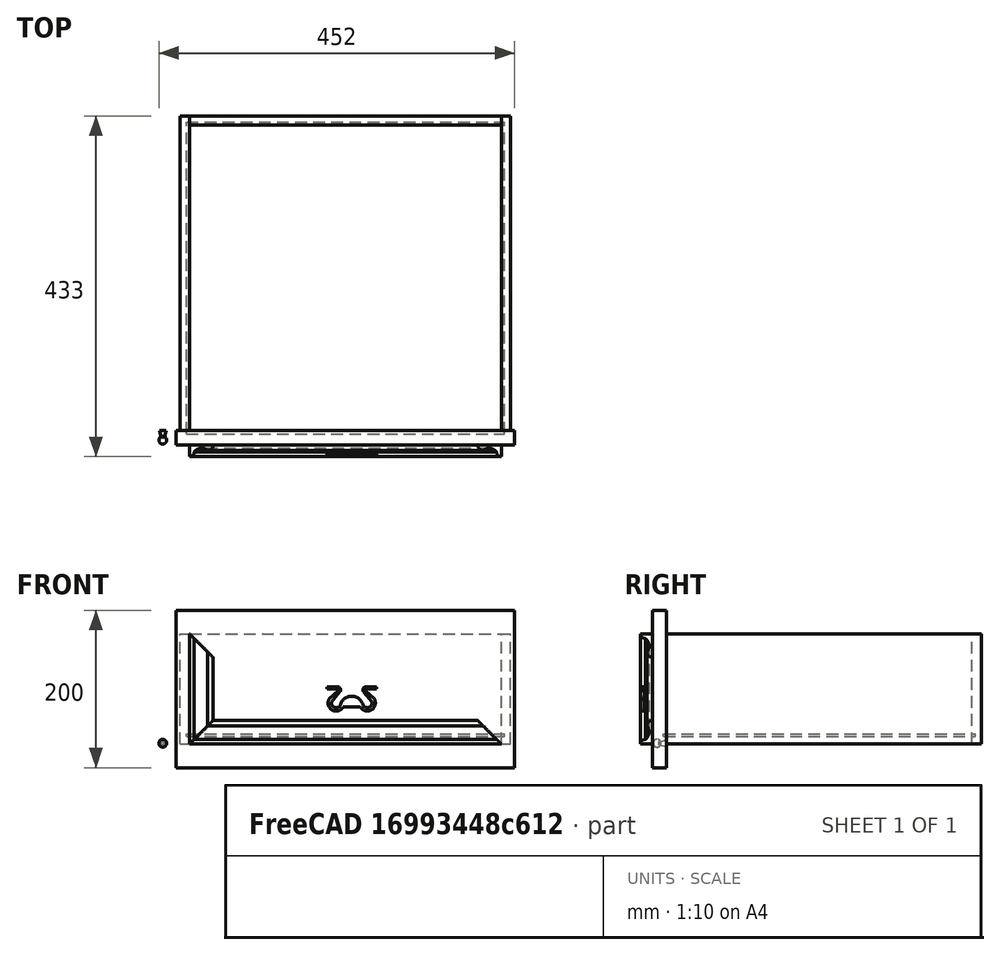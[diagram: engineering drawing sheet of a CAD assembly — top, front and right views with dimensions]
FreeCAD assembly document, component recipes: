
FREECAD ASSEMBLY — COMPONENT RECIPES ("Drawer_002")

This assembly document has 6 components, labeled P0..P5 below (a component is one placed body or linked part). 3 of them carry a construction recipe — the FreeCAD feature program that regenerates the part from scratch, quoted from this document or its linked companion documents; the rest are supplied as boundary geometry only. No exploded tour is included for this assembly.
COMPONENT P0 — geometry summary ("Handle, Pin, Right"; no construction recipe available for this part):
  bounding box: 17.0 x 10.0 x 10.0 mm
  tessellated surface: 9,562 triangles
  volume: 817 mm^3 (48% of its bounding box)
  symmetry: revolution-symmetric about the y axis through its bounding-box center; mirror-symmetric across its x mid-plane, z mid-plane
COMPONENT P1 — geometry summary ("Link, Decoration, Top"; no construction recipe available for this part):
  bounding box: 396.0 x 30.0 x 15.0 mm
  tessellated surface: 406 triangles
  volume: 79802 mm^3 (45% of its bounding box)
  symmetry: mirror-symmetric across its x mid-plane
COMPONENT P2 — geometry summary ("Link, Decoration, Right"; no construction recipe available for this part):
  bounding box: 140.0 x 30.0 x 15.0 mm
  tessellated surface: 388 triangles
  volume: 24915 mm^3 (40% of its bounding box)
  symmetry: mirror-symmetric across its z mid-plane
COMPONENT P3 — recipe-attached ("Part, Handle", modeled in this document).
Construction recipe (the document's own serialized feature program — sketch geometry with constraints, then the solid features built on it; lengths are millimeters unless a unit is written):

FEATURE [Sketcher::SketchObject] Sketch006  label="Pattern, Handle"
  ArcFitTolerance = 0
  AttachmentOffset = pos=(210,70,28) rot=(0,0,1;0rad)
  AttachmentSupport = -> [XZ_Plane006]
  ExternalTypes = [0]
  FullyConstrained = true
  MakeInternals = false
  MapMode = 5
  Placement = pos=(210,-28,70) rot=(1,0,0;1.5708rad)
  _ExternalGeoVersion = 0
  expr: .AttachmentOffset.Base.x = <<settings>>.dwidth / 2
  expr: .AttachmentOffset.Base.y = <<settings>>.dheight / 2
  expr: .AttachmentOffset.Base.z = <<settings>>.fthick + 10 mm
  sketch-geometry (20):
    g0: LineSegment StartX=-31.5 StartY=2.62 StartZ=0 EndX=-17.57 EndY=2.62 EndZ=0
    g1: LineSegment StartX=-31.5 StartY=0 StartZ=0 EndX=-17.3512 EndY=0 EndZ=0
    g2: LineSegment StartX=-16.85 StartY=-2.15 StartZ=0 EndX=-28.7075 EndY=-12.82 EndZ=0
    g3: LineSegment StartX=-15.2654 StartY=-4.11 StartZ=0 EndX=-25.6265 EndY=-16.59 EndZ=0
    g4: LineSegment StartX=15.2654 StartY=-4.11 StartZ=0 EndX=25.6265 EndY=-16.59 EndZ=0
    g5: LineSegment StartX=16.85 StartY=-2.15 StartZ=0 EndX=28.7075 EndY=-12.82 EndZ=0
    g6: LineSegment StartX=17.57 StartY=2.62 StartZ=0 EndX=31.5 EndY=2.62 EndZ=0
    g7: LineSegment StartX=17.3512 StartY=0 StartZ=0 EndX=31.5 EndY=0 EndZ=0
    g8: LineSegment StartX=-10.78 StartY=-22.72 StartZ=0 EndX=10.78 EndY=-22.72 EndZ=0
    g9: LineSegment StartX=-31.5 StartY=2.62 StartZ=0 EndX=-31.5 EndY=0 EndZ=0
    g10: LineSegment StartX=31.5 StartY=2.62 StartZ=0 EndX=31.5 EndY=0 EndZ=0
    g11: ArcOfCircle CenterX=-17.98 CenterY=-1.28 CenterZ=0 NormalX=0 NormalY=0 NormalZ=1 AngleXU=0 Radius=3.92149 StartAngle=5.47698 EndAngle=7.74924
    g12: ArcOfCircle CenterX=-17.98 CenterY=-1.28 CenterZ=0 NormalX=0 NormalY=0 NormalZ=1 AngleXU=0 Radius=1.42611 StartAngle=5.62706 EndAngle=7.39735
    g13: ArcOfCircle CenterX=-19.81 CenterY=-17.89 CenterZ=0 NormalX=0 NormalY=0 NormalZ=1 AngleXU=0 Radius=10.2406 StartAngle=2.62366 EndAngle=5.79202
    g14: ArcOfCircle CenterX=19.81 CenterY=-17.89 CenterZ=0 NormalX=0 NormalY=0 NormalZ=1 AngleXU=0 Radius=10.2406 StartAngle=3.63276 EndAngle=6.80112
    g15: ArcOfCircle CenterX=17.98 CenterY=-1.28 CenterZ=0 NormalX=0 NormalY=0 NormalZ=1 AngleXU=0 Radius=3.92149 StartAngle=1.67554 EndAngle=3.9478
    g16: ArcOfCircle CenterX=17.98 CenterY=-1.28 CenterZ=0 NormalX=0 NormalY=0 NormalZ=1 AngleXU=0 Radius=1.42611 StartAngle=2.02742 EndAngle=3.79772
    g17: ArcOfCircle CenterX=0 CenterY=-24.02 CenterZ=0 NormalX=0 NormalY=0 NormalZ=1 AngleXU=0 Radius=14.7824 StartAngle=0.285269 EndAngle=2.85632
    g18: ArcOfCircle CenterX=-19.81 CenterY=-17.89 CenterZ=0 NormalX=0 NormalY=0 NormalZ=1 AngleXU=0 Radius=5.95999 StartAngle=2.9217 EndAngle=5.94631
    g19: ArcOfCircle CenterX=19.81 CenterY=-17.89 CenterZ=0 NormalX=0 NormalY=0 NormalZ=1 AngleXU=0 Radius=5.95999 StartAngle=3.47847 EndAngle=6.50307
  constraints (66):
    c: Horizontal(g0)
    c: Horizontal(g1)
    c: Horizontal(g6)
    c: Horizontal(g7)
    c: Horizontal(g8)
    c: Coincident(g9,g0)
    c: Coincident(g9,g1)
    c: Vertical(g9)
    c: Coincident(g10,g6)
    c: Vertical(g10)
    c: Coincident(g10,g7)
    c: Coincident(g11,g0)
    c: Coincident(g11,g3)
    c: Coincident(g12,g1)
    c: Coincident(g12,g2)
    c: Coincident(g13,g2)
    c: Coincident(g13,g8)
    c: Coincident(g14,g5)
    c: Coincident(g14,g8)
    c: Coincident(g15,g4)
    c: Coincident(g15,g6)
    c: Coincident(g16,g7)
    c: Coincident(g16,g5)
    c: Coincident(g18,g3)
    c: Coincident(g18,g17)
    c: Coincident(g19,g17)
    c: Coincident(g19,g4)
    c: Coincident(g15,g16)
    c: Coincident(g11,g12)
    c: Horizontal(g2,g5)
    c: Horizontal(g3,g4)
    c: Horizontal(g0,g6)
    c: Horizontal(g1,g7)
    c: Horizontal(g5,g2)
    c: Horizontal(g13,g14)
    c: Horizontal(g18,g19)
    c: Horizontal(g17,g17)
    c: Horizontal(g3,g4)
    c: PointOnObject(g17,g-2)
    c: Equal(g11,g15)
    c: Equal(g0,g6)
    c: Equal(g1,g7)
    c: Equal(g3,g4)
    c: Equal(g18,g19)
    c: Equal(g2,g5)
    c: Equal(g13,g14)
    c: Horizontal(g11,g15)
    c: Coincident(g13,g18)
    c: PointOnObject(g7,g-1)
    c: DistanceY(g17,g-1) = 24.02
    c: DistanceY(g14,g-1) = 17.89
    c: DistanceY(g2,g-1) = 12.82
    c: DistanceY(g3,g-1) = 16.59
    c: DistanceY(g8,g-1) = 22.72
    c: DistanceX(g8,g-1) = 10.78
    c: DistanceY(g3,g-1) = 4.11
    c: DistanceY(g2,g-1) = 2.15
    c: DistanceY(g-1,g0) = 2.62
    c: DistanceX(g0,g6) = 63
    c: DistanceX(g13,g14) = 39.62
    c: DistanceX(g17,g17) = 28.37
    c: DistanceY(g17,g-1) = 19.86
    c: DistanceX(g11,g-1) = 17.98
    c: DistanceX(g0,g-1) = 17.57
    c: DistanceX(g2,g-1) = 16.85
    c: DistanceY(g11,g-1) = 1.28
FEATURE [PartDesign::Pad] Pad006  label="Handle"
  Direction = (0,-1,2e-16)
  Length = 5
  Length2 = 10
  Placement = pos=(0,0,0) rot=(1,0,0;1.5708rad)
  Profile = -> Sketch006
  ReferenceAxis = -> Sketch006 [N_Axis]
  SideType = 0
  Suppressed = false
  Type = 0
  Type2 = 0
FEATURE [PartDesign::Body] Body006  label="Body, Handle"
  AllowCompound = true
  Group = -> [Sketch006,Pad006]
  Origin = -> Origin007
  Tip = -> Pad006
COMPONENT P4 — recipe-attached ("Part, Decoration, Bottom", modeled in this document).
Construction recipe (the document's own serialized feature program — sketch geometry with constraints, then the solid features built on it; lengths are millimeters unless a unit is written):

FEATURE [Sketcher::SketchObject] Sketch  label="Pattern, Decoration, Bottom"
  ArcFitTolerance = 0
  AttachmentOffset = pos=(-18,0,4) rot=(0,0,1;0rad)
  AttachmentSupport = -> [YZ_Plane008]
  ExternalTypes = [0]
  FullyConstrained = true
  MakeInternals = false
  MapMode = 5
  Placement = pos=(4,-18,0) rot=(0.57735,0.57735,0.57735;2.0944rad)
  _ExternalGeoVersion = 0
  expr: .AttachmentOffset.Base.x = -<<settings>>.fthick
  expr: .AttachmentOffset.Base.z = <<settings>>.bsink
  sketch-geometry (5):
    g0: LineSegment StartX=4e-16 StartY=30 StartZ=0 EndX=4e-16 EndY=0 EndZ=0
    g1: LineSegment StartX=4e-16 StartY=0 StartZ=0 EndX=-15 EndY=0 EndZ=0
    g2: ArcOfCircle CenterX=0 CenterY=23 CenterZ=0 NormalX=0 NormalY=0 NormalZ=1 AngleXU=0 Radius=7 StartAngle=1.5708 EndAngle=3.14159
    g3: ArcOfCircle CenterX=-16.3537 CenterY=15.4828 CenterZ=0 NormalX=0 NormalY=0 NormalZ=1 AngleXU=0 Radius=12 StartAngle=5.372 EndAngle=6.96016
    g4: ArcOfCircle CenterX=-9 CenterY=0 CenterZ=0 NormalX=0 NormalY=0 NormalZ=1 AngleXU=0 Radius=6 StartAngle=1.5708 EndAngle=3.14159
  constraints (17):
    c: Vertical(g0)
    c: Coincident(g1,g0)
    c: Horizontal(g1)
    c: Coincident(g2,g0)
    c: Coincident(g3,g2)
    c: Coincident(g4,g3)
    c: Coincident(g4,g1)
    c: DistanceY(g0,g0) = 30
    c: DistanceX(g1,g1) = 15
    c: Coincident(g0,g-1)
    c: PointOnObject(g2,g0)
    c: PointOnObject(g4,g1)
    c: Radius(g2) = 7
    c: Radius(g3) = 12
    c: Radius(g4) = 6
    c: Vertical(g3,g4)
    c: Horizontal(g2,g2)
FEATURE [PartDesign::Pad] Pad  label="Decoration, Bottom"
  Direction = (1,0,0)
  Length = 396
  Length2 = 10
  Placement = pos=(0,0,0) rot=(0.57735,0.57735,0.57735;2.0944rad)
  Profile = -> Sketch
  ReferenceAxis = -> Sketch [N_Axis]
  SideType = 0
  Suppressed = false
  Type = 0
  Type2 = 0
  expr: Length = <<settings>>.dwidth - 2 * <<settings>>.dthick
FEATURE [PartDesign::Body] Body  label="Body, Decoration, Bottom"
  AllowCompound = true
  Group = -> [Sketch,Pad]
  Origin = -> Origin009
  Tip = -> Pad
FEATURE [Sketcher::SketchObject] Sketch007  label="Pattern, Decoration, Bottom, Cut, Left"
  ArcFitTolerance = 0
  AttachmentOffset = pos=(4,0,18) rot=(0,0,1;0rad)
  AttachmentSupport = -> [XZ_Plane009]
  ExternalTypes = [0]
  FullyConstrained = true
  MakeInternals = false
  MapMode = 5
  Placement = pos=(4,-18,4e-15) rot=(1,0,0;1.5708rad)
  _ExternalGeoVersion = 0
  expr: .AttachmentOffset.Base.x = <<settings>>.bsink
  expr: .AttachmentOffset.Base.z = <<settings>>.fthick
  sketch-geometry (3):
    g0: LineSegment StartX=0 StartY=0 StartZ=0 EndX=40 EndY=40 EndZ=0
    g1: LineSegment StartX=40 StartY=40 StartZ=0 EndX=0 EndY=40 EndZ=0
    g2: LineSegment StartX=0 StartY=40 StartZ=0 EndX=0 EndY=0 EndZ=0
  constraints (8):
    c: Coincident(g0,g1)
    c: Horizontal(g1)
    c: Coincident(g1,g2)
    c: Coincident(g2,g0)
    c: Coincident(g0,g-1)
    c: Vertical(g2)
    c: Equal(g2,g1)
    c: DistanceY(g2,g2) = 40
FEATURE [PartDesign::Pad] Pad007  label="Decoration, Bottom, Cut, Left"
  Direction = (0,-1,2e-16)
  Length = 40
  Length2 = 10
  Placement = pos=(0,0,0) rot=(1,0,0;1.5708rad)
  Profile = -> Sketch007
  ReferenceAxis = -> Sketch007 [N_Axis]
  SideType = 0
  Suppressed = false
  Type = 0
  Type2 = 0
FEATURE [PartDesign::Body] Body007  label="Body, Decoration, Bottom, Cut, Left"
  AllowCompound = true
  Group = -> [Sketch007,Pad007]
  Origin = -> Origin010
  Tip = -> Pad007
FEATURE [Sketcher::SketchObject] Sketch008  label="Pattern, Decoration, Bottom, Cut, Right"
  ArcFitTolerance = 0
  AttachmentOffset = pos=(400,0,18) rot=(0,0,1;0rad)
  AttachmentSupport = -> [XZ_Plane010]
  ExternalTypes = [0]
  FullyConstrained = true
  MakeInternals = false
  MapMode = 5
  Placement = pos=(400,-18,4e-15) rot=(1,0,0;1.5708rad)
  _ExternalGeoVersion = 0
  expr: .AttachmentOffset.Base.x = <<settings>>.bsink + <<settings>>.dwidth - 2 * <<settings>>.dthick
  expr: .AttachmentOffset.Base.z = <<settings>>.fthick
  sketch-geometry (3):
    g0: LineSegment StartX=-40 StartY=40 StartZ=0 EndX=0 EndY=0 EndZ=0
    g1: LineSegment StartX=0 StartY=0 StartZ=0 EndX=0 EndY=40 EndZ=0
    g2: LineSegment StartX=0 StartY=40 StartZ=0 EndX=-40 EndY=40 EndZ=0
  constraints (8):
    c: Coincident(g0,g-1)
    c: Coincident(g0,g1)
    c: PointOnObject(g1,g-2)
    c: Coincident(g1,g2)
    c: Coincident(g2,g0)
    c: Horizontal(g2)
    c: Equal(g2,g1)
    c: DistanceY(g1,g1) = 40
FEATURE [PartDesign::Pad] Pad008  label="Decoration, Bottom, Cut, Right"
  Direction = (0,-1,2e-16)
  Length = 40
  Length2 = 10
  Placement = pos=(0,0,0) rot=(1,0,0;1.5708rad)
  Profile = -> Sketch008
  ReferenceAxis = -> Sketch008 [N_Axis]
  SideType = 0
  Suppressed = false
  Type = 0
  Type2 = 0
FEATURE [PartDesign::Body] Body008  label="Body, Decoration, Bottom, Cut, Right"
  AllowCompound = true
  Group = -> [Sketch008,Pad008]
  Origin = -> Origin011
  Tip = -> Pad008
COMPONENT P5 — recipe-attached ("Part, Decoration, Left", modeled in this document).
Construction recipe (the document's own serialized feature program — sketch geometry with constraints, then the solid features built on it; lengths are millimeters unless a unit is written):

FEATURE [Sketcher::SketchObject] Sketch009  label="Pattern, Decoration, Left"
  ArcFitTolerance = 0
  AttachmentOffset = pos=(4,-18,0) rot=(0,0,1;0rad)
  AttachmentSupport = -> [XY_Plane012]
  ExternalTypes = [0]
  FullyConstrained = true
  MakeInternals = false
  MapMode = 5
  Placement = pos=(4,-18,0) rot=(0,0,1;0rad)
  _ExternalGeoVersion = 0
  expr: .AttachmentOffset.Base.x = <<settings>>.bsink
  expr: .AttachmentOffset.Base.y = -<<settings>>.fthick
  sketch-geometry (5):
    g0: LineSegment StartX=30 StartY=-1.8e-15 StartZ=0 EndX=0 EndY=-1.8e-15 EndZ=0
    g1: LineSegment StartX=0 StartY=-15 StartZ=0 EndX=0 EndY=-1.8e-15 EndZ=0
    g2: ArcOfCircle CenterX=0 CenterY=-9 CenterZ=0 NormalX=0 NormalY=0 NormalZ=1 AngleXU=0 Radius=6 StartAngle=4.71239 EndAngle=6.28319
    g3: ArcOfCircle CenterX=15.4828 CenterY=-16.3537 CenterZ=0 NormalX=0 NormalY=0 NormalZ=1 AngleXU=0 Radius=12 StartAngle=0.893826 EndAngle=2.48198
    g4: ArcOfCircle CenterX=23 CenterY=0 CenterZ=0 NormalX=0 NormalY=0 NormalZ=1 AngleXU=0 Radius=7 StartAngle=4.71239 EndAngle=6.28319
  constraints (17):
    c: Vertical(g1)
    c: Coincident(g0,g1)
    c: Horizontal(g0)
    c: Coincident(g0,g-1)
    c: DistanceY(g1,g1) = 15
    c: DistanceX(g0,g0) = 30
    c: Coincident(g2,g1)
    c: Coincident(g3,g2)
    c: Coincident(g4,g3)
    c: Coincident(g4,g0)
    c: PointOnObject(g4,g0)
    c: PointOnObject(g2,g1)
    c: Radius(g2) = 6
    c: Radius(g3) = 12
    c: Radius(g4) = 7
    c: Horizontal(g2,g2)
    c: Vertical(g3,g4)
FEATURE [PartDesign::Pad] Pad009  label="Decoration, Left"
  Direction = (0,0,1)
  Length = 140
  Length2 = 10
  Profile = -> Sketch009
  ReferenceAxis = -> Sketch009 [N_Axis]
  SideType = 0
  Suppressed = false
  Type = 0
  Type2 = 0
  expr: Length = <<settings>>.dheight
FEATURE [PartDesign::Body] Body009  label="Body, Decoration, Left"
  AllowCompound = true
  Group = -> [Sketch009,Pad009]
  Origin = -> Origin013
  Tip = -> Pad009
FEATURE [Sketcher::SketchObject] Sketch010  label="Pattern, Decoration, Left, Cut, Bottom"
  ArcFitTolerance = 0
  AttachmentOffset = pos=(4,0,18) rot=(0,0,1;0rad)
  AttachmentSupport = -> [XZ_Plane013]
  ExternalTypes = [0]
  FullyConstrained = true
  MakeInternals = false
  MapMode = 5
  Placement = pos=(4,-18,4e-15) rot=(1,0,0;1.5708rad)
  _ExternalGeoVersion = 0
  expr: .AttachmentOffset.Base.x = <<settings>>.bsink
  expr: .AttachmentOffset.Base.z = <<settings>>.fthick
  sketch-geometry (3):
    g0: LineSegment StartX=0 StartY=0 StartZ=0 EndX=40 EndY=40 EndZ=0
    g1: LineSegment StartX=40 StartY=40 StartZ=0 EndX=40 EndY=0 EndZ=0
    g2: LineSegment StartX=40 StartY=0 StartZ=0 EndX=0 EndY=0 EndZ=0
  constraints (8):
    c: Coincident(g-1,g0)
    c: Coincident(g0,g1)
    c: PointOnObject(g1,g-1)
    c: Vertical(g1)
    c: Coincident(g1,g2)
    c: Coincident(g2,g0)
    c: Equal(g1,g2)
    c: DistanceY(g1,g1) = 40
FEATURE [PartDesign::Pad] Pad010  label="Decoration, Left, Cut, Bottom"
  Direction = (0,-1,2e-16)
  Length = 40
  Length2 = 10
  Placement = pos=(0,0,0) rot=(1,0,0;1.5708rad)
  Profile = -> Sketch010
  ReferenceAxis = -> Sketch010 [N_Axis]
  SideType = 0
  Suppressed = false
  Type = 0
  Type2 = 0
FEATURE [PartDesign::Body] Body010  label="Body, Decoration, Left, Cut, Bottom"
  AllowCompound = true
  Group = -> [Sketch010,Pad010]
  Origin = -> Origin014
  Tip = -> Pad010
FEATURE [Sketcher::SketchObject] Sketch011  label="Pattern, Decoration, Left, Cut, Top"
  ArcFitTolerance = 0
  AttachmentOffset = pos=(4,140,18) rot=(0,0,1;0rad)
  AttachmentSupport = -> [XZ_Plane014]
  ExternalTypes = [0]
  FullyConstrained = true
  MakeInternals = false
  MapMode = 5
  Placement = pos=(4,-18,140) rot=(1,0,0;1.5708rad)
  _ExternalGeoVersion = 0
  expr: .AttachmentOffset.Base.x = <<settings>>.bsink
  expr: .AttachmentOffset.Base.y = <<settings>>.dheight
  expr: .AttachmentOffset.Base.z = <<settings>>.fthick
  sketch-geometry (3):
    g0: LineSegment StartX=0 StartY=0 StartZ=0 EndX=40 EndY=-40 EndZ=0
    g1: LineSegment StartX=40 StartY=-40 StartZ=0 EndX=40 EndY=0 EndZ=0
    g2: LineSegment StartX=40 StartY=0 StartZ=0 EndX=0 EndY=0 EndZ=0
  constraints (8):
    c: Coincident(g-1,g0)
    c: Coincident(g0,g1)
    c: PointOnObject(g1,g-1)
    c: Vertical(g1)
    c: Coincident(g1,g2)
    c: Coincident(g2,g0)
    c: Equal(g1,g2)
    c: DistanceY(g1,g1) = 40
FEATURE [PartDesign::Pad] Pad011  label="Decoration, Left, Cut, Top"
  Direction = (0,-1,2e-16)
  Length = 40
  Length2 = 10
  Placement = pos=(0,0,0) rot=(1,0,0;1.5708rad)
  Profile = -> Sketch011
  ReferenceAxis = -> Sketch011 [N_Axis]
  SideType = 0
  Suppressed = false
  Type = 0
  Type2 = 0
FEATURE [PartDesign::Body] Body011  label="Body, Decoration, Left, Cut, Top"
  AllowCompound = true
  Group = -> [Sketch011,Pad011]
  Origin = -> Origin015
  Tip = -> Pad011
PROVENANCE & LICENSES
A FreeCAD (.FCStd) document from a public repository crawl; recipes are the document's own serialized feature recipes (and, for linked parts, companion documents' recipes).
License: mit.
